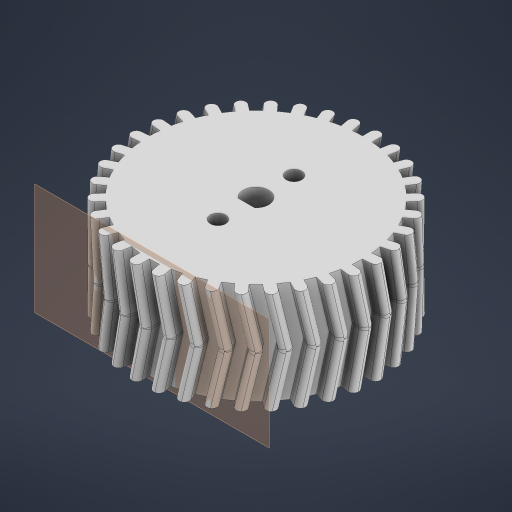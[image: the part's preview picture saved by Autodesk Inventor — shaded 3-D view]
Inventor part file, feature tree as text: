
AUTODESK INVENTOR PART (.ipt)
format: ipt  version: 2023 (Build 270158030, 158C)  size: 745,472 bytes
history: native  units: in
note: dims shown in document units (in); Inventor stores cm internally (conversion verified against a paired STEP export)
features: extrude x5, sketch x5, plane x1, fillet x1, pattern_circular x1
ambient origin geometry x8: Origin, YZ Plane, XZ Plane, XY Plane, X Axis, Y Axis, Z Axis, Center Point
bodies: Solid1 (feature_tree)
feature tree (13):
  extrude  "Extrusion1"  Depth=0.7874in TaperAngle=0.0deg
  plane  "Work Plane1"
  extrude  "Extrusion2"  Depth=0.8071in
  extrude  "Extrusion3"  Depth=0.0787in
  fillet  "Fillet3"  Radius=0.1181in
  pattern_circular  "Circular Pattern2"  [2 undecoded]
  extrude  "Extrusion5"  Depth=0.0394in
  extrude  "Extrusion6"  Depth=0.5118in TaperAngle=360.0deg
  sketch  "Sketch3"  dims[d0=1.6535in d1=0.7874in d2=0.0in]
  sketch  "Sketch8"  dims[d3=0.8071in d4=0.0787in]
  sketch  "Sketch10"  dims[d5=0.0787in d6=0.0787in d7=0.1181in d8=0.0in]
  sketch  "Sketch13"  dims[d17=0.1969in]
  sketch  "Sketch14"  dims[d18=0.1732in d19=0.8268in d20=0.0in d23=0.0394in d24=13.189in d25=360.0deg d30=0.874in d31=0.2756in d32=0.0in d33=0.1181in d34=0.1181in d35=0.5906in d37=0.2953in d38=0.5118in d39=0.0in d26=0.0in]
note: 2 required parameter values undecoded (feature->parameter linkage not recoverable at this tier; creation-order binding heuristic only, values carry confidence <= 0.55)
